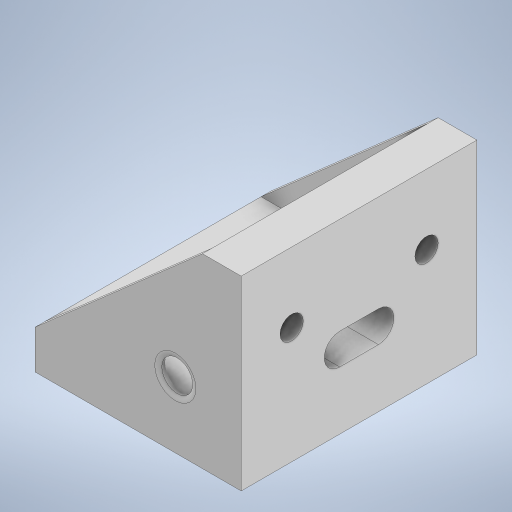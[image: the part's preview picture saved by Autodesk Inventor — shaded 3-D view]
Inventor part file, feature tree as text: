
AUTODESK INVENTOR PART (.ipt)
format: ipt  version: 2024 (Build 280153000, 153)  size: 375,296 bytes
history: native  units: mm
features: extrude x10, sketch x10, projected_geometry x8, fillet x1
ambient origin geometry x8: Origin, YZ Plane, XZ Plane, XY Plane, X Axis, Y Axis, Z Axis, Center Point
bodies: Solid1 (feature_tree)
feature tree (29):
  extrude  "Extrusion1"  Depth=10.0mm
  extrude  "Extrusion2"  Depth=6.35mm
  extrude  "Extrusion3"  Depth=10.0mm
  extrude  "Extrusion4"  Depth=25.4mm
  extrude  "Extrusion5"  Depth=10.0mm
  extrude  "Extrusion6"  Depth=38.0mm
  extrude  "Extrusion7"  Depth=34.8mm
  extrude  "Extrusion8"  Depth=20.0mm
  extrude  "Extrusion9"  Depth=8.0mm
  extrude  "Extrusion10"  Depth=2.0mm TaperAngle=0.0deg
  fillet  "Fillet1"  Radius=10.0mm
  sketch  "Sketch1"  dims[d0=50.8mm d2=10.0mm]
  sketch  "Sketch2"  dims[d3=6.35mm d4=6.35mm]
  sketch  "Sketch3"  dims[d6=20.0mm d7=10.0mm]
  projected_geometry  "Projected Loop1"
  sketch  "Sketch4"  dims[d8=13.175mm d9=25.4mm]
  projected_geometry  "Projected Loop2"
  sketch  "Sketch5"  dims[d10=10.0mm d11=0.0mm d12=10.0mm]
  projected_geometry  "Projected Loop3"
  sketch  "Sketch6"  dims[d13=38.0mm d14=0.0mm d15=2.84mm]
  projected_geometry  "Projected Loop4"
  sketch  "Sketch7"  dims[d16=2.84mm d17=34.8mm]
  projected_geometry  "Projected Loop5"
  sketch  "Sketch8"  dims[d18=0.0mm d19=20.0mm]
  projected_geometry  "Projected Loop6"
  sketch  "Sketch9"  dims[d20=8.0mm d21=8.0mm]
  projected_geometry  "Projected Loop7"
  sketch  "Sketch10"  dims[d22=50.8mm d23=36.0mm d24=0.0mm d25=10.0mm d26=10.0mm d27=10.0mm d28=10.0mm d29=6.0mm d30=0.0mm d31=6.0mm d32=6.0mm d33=5.0mm d34=0.0mm d35=8.0mm d36=8.0mm d37=0.0mm d38=10.0mm d39=5.0mm d40=25.4mm d41=9.0mm d43=25.4mm d44=2.5mm d45=0.0mm d46=2.5mm d47=0.0mm d48=2.5mm d49=0.0mm d50=2.5mm d51=0.0mm d52=7.0mm d53=7.0mm d54=8.0mm d55=0.0mm d56=0.0mm d57=2.0mm]
  projected_geometry  "Projected Loop8"
